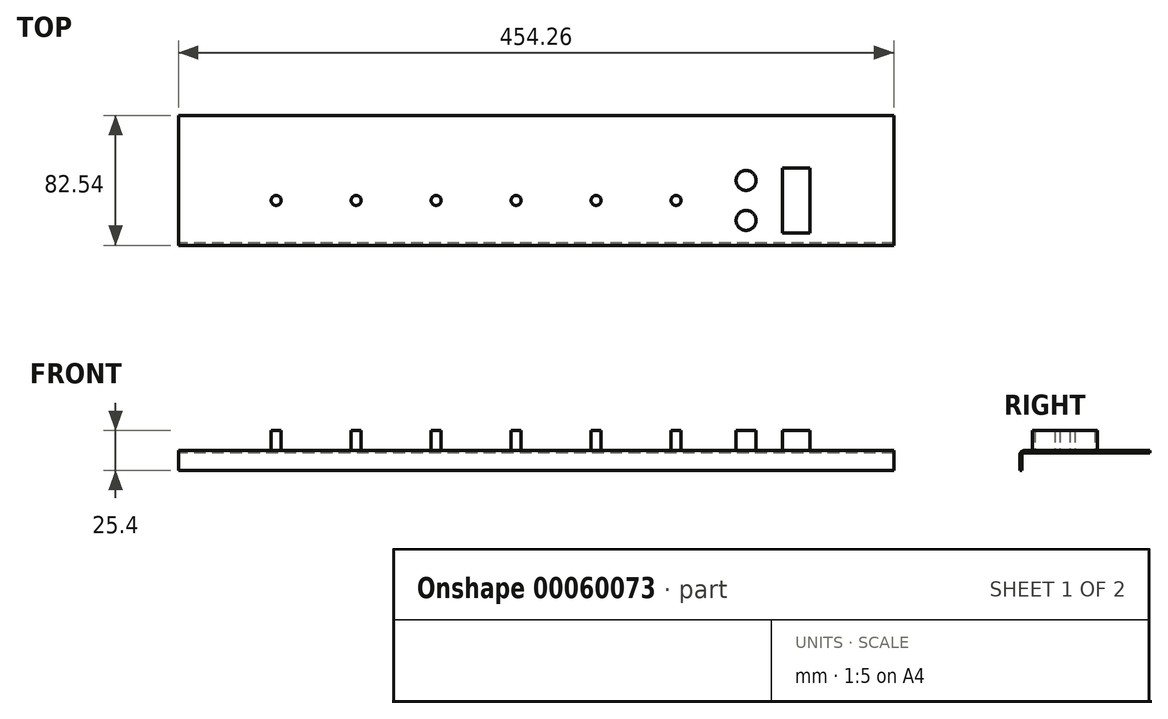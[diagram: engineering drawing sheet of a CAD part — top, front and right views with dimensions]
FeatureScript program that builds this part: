
annotation { "Feature Type Name" : "Feature", "Feature Type Description" : "" }
export const myFeature = defineFeature(function(context is Context, id is Id, definition is map)
    precondition{}
    {
        {
            var Q0;
            Q0=qCreatedBy(makeId("Top.planeOp"),FACE);
            var sketch = newSketch(context, id + "F0", { "sketchPlane" : qUnion([Q0])});
            skLineSegment(sketch, "E0.rect.bottom", {"start": v(241.3, -41.27) * mm, "end": v(-241.3, -41.28) * mm});
            skLineSegment(sketch, "E0.rect.top", {"start": v(241.3, 41.28) * mm, "end": v(-241.3, 41.27) * mm});
            skLineSegment(sketch, "E0.rect.left", {"start": v(241.3, -41.27) * mm, "end": v(241.3, 41.28) * mm});
            skLineSegment(sketch, "E0.rect.right", {"start": v(-241.3, -41.28) * mm, "end": v(-241.3, 41.27) * mm});
            skPoint(sketch, "E0.rect.middle", {"position": v(0, 0) * mm});
            skSolve(sketch);
        }
        {
            var Q0;
            Q0 = qSketchRegion(id + "F0", true);
            extrude(context, id + "F1", {"entities" : qUnion([Q0]), "oppositeDirection" : true, "depth" : 12.7 * mm});
        }
        {
            var Q0;
            Q0=makeQuery(id+"F1.opExtrude","CAP_EDGE",EDGE,{"disambiguationData":[OSD([sQuery(id+"F0.wireOp",EDGE,"E0.rect.bottom")])],"isStart":true});
            fillet(context, id + "F2", {"entities" : qUnion([Q0]), "radius" : 3.17 * mm, "tangentPropagation" : true, "allowEdgeOverflow" : false});
        }
        {
            var Q0;
            Q0=makeQuery(id+"F1.opExtrude","CAP_FACE",FACE,{"disambiguationData":[OSD([sQuery(id+"F0.wireOp",EDGE,"E0.rect.bottom"),sQuery(id+"F0.wireOp",EDGE,"E0.rect.top"),sQuery(id+"F0.wireOp",EDGE,"E0.rect.left"),sQuery(id+"F0.wireOp",EDGE,"E0.rect.right")])],"isStart":false});
            var Q1;
            Q1=makeQuery(id+"F1.opExtrude","SWEPT_FACE",FACE,{"disambiguationData":[OSD([sQuery(id+"F0.wireOp",EDGE,"E0.rect.left")])]});
            var Q2;
            Q2=makeQuery(id+"F1.opExtrude","SWEPT_FACE",FACE,{"disambiguationData":[OSD([sQuery(id+"F0.wireOp",EDGE,"E0.rect.top")])]});
            var Q3;
            Q3=makeQuery(id+"F1.opExtrude","SWEPT_FACE",FACE,{"disambiguationData":[OSD([sQuery(id+"F0.wireOp",EDGE,"E0.rect.right")])]});
            shell(context, id + "F3", {"entities" : qUnion([Q0, Q1, Q2, Q3]), "thickness" : 1.52 * mm});
        }
        {
            var Q0;
            Q0=makeQuery(id+"F1.opExtrude","CAP_FACE",FACE,{"disambiguationData":[OSD([sQuery(id+"F0.wireOp",EDGE,"E0.rect.bottom"),sQuery(id+"F0.wireOp",EDGE,"E0.rect.top"),sQuery(id+"F0.wireOp",EDGE,"E0.rect.left"),sQuery(id+"F0.wireOp",EDGE,"E0.rect.right")])],"isStart":true});
            var sketch = newSketch(context, id + "F4", { "sketchPlane" : qUnion([Q0])});
            skCircle(sketch, "E1", {"center": v(-114.3, -12.7) * mm, "radius": 3.18 * mm});
            skCircle(sketch, "E2", {"center": v(-63.5, -12.7) * mm, "radius": 3.18 * mm});
            skCircle(sketch, "E3", {"center": v(-12.7, -12.7) * mm, "radius": 3.18 * mm});
            skCircle(sketch, "E4", {"center": v(38.1, -12.7) * mm, "radius": 3.18 * mm});
            skCircle(sketch, "E5", {"center": v(88.9, -12.7) * mm, "radius": 3.18 * mm});
            skCircle(sketch, "E6", {"center": v(-165.1, -12.7) * mm, "radius": 3.18 * mm});
            skCircle(sketch, "E7", {"center": v(133.35, 0) * mm, "radius": 6.35 * mm});
            skCircle(sketch, "E8", {"center": v(133.35, -25.4) * mm, "radius": 6.35 * mm});
            skLineSegment(sketch, "E9.bottom", {"start": v(173.83, 7.94) * mm, "end": v(156.37, 7.94) * mm});
            skLineSegment(sketch, "E9.top", {"start": v(173.83, -33.34) * mm, "end": v(156.37, -33.34) * mm});
            skLineSegment(sketch, "E9.left", {"start": v(173.83, 7.94) * mm, "end": v(173.83, -33.34) * mm});
            skLineSegment(sketch, "E9.right", {"start": v(156.37, 7.94) * mm, "end": v(156.37, -33.34) * mm});
            skLineSegment(sketch, "E10", {"start": v(-165.1, -12.7) * mm, "end": v(-114.3, -12.7) * mm, "construction": true});
            skLineSegment(sketch, "E11", {"start": v(-63.5, -12.7) * mm, "end": v(-12.7, -12.7) * mm, "construction": true});
            skLineSegment(sketch, "E12", {"start": v(38.1, -12.7) * mm, "end": v(88.9, -12.7) * mm, "construction": true});
            skLineSegment(sketch, "E13", {"start": v(38.1, -12.7) * mm, "end": v(-12.7, -12.7) * mm, "construction": true});
            skLineSegment(sketch, "E14", {"start": v(-63.5, -12.7) * mm, "end": v(-114.3, -12.7) * mm, "construction": true});
            skLineSegment(sketch, "E15", {"start": v(88.9, -12.7) * mm, "end": v(156.37, -12.7) * mm, "construction": true});
            skLineSegment(sketch, "E16", {"start": v(165.1, -33.34) * mm, "end": v(165.1, 7.94) * mm, "construction": true});
            skSolve(sketch);
        }
        {
            var Q0;
            Q0 = qSketchRegion(id + "F4", true);
            extrude(context, id + "F5", {"entities" : qUnion([Q0]), "operationType" : NewBodyOperationType.ADD, "depth" : 12.7 * mm});
        }
        {
            var Q0;
            Q0=makeQuery(id+"F1.opExtrude","CAP_FACE",FACE,{"disambiguationData":[OSD([sQuery(id+"F0.wireOp",EDGE,"E0.rect.bottom"),sQuery(id+"F0.wireOp",EDGE,"E0.rect.top"),sQuery(id+"F0.wireOp",EDGE,"E0.rect.left"),sQuery(id+"F0.wireOp",EDGE,"E0.rect.right")])],"isStart":true});
            var sketch = newSketch(context, id + "F6", { "sketchPlane" : qUnion([Q0])});
            skLineSegment(sketch, "E17.bottom", {"start": v(-241.3, 41.27) * mm, "end": v(-227.13, 41.27) * mm});
            skLineSegment(sketch, "E17.top", {"start": v(-241.3, -41.28) * mm, "end": v(-227.13, -41.28) * mm});
            skLineSegment(sketch, "E17.left", {"start": v(-241.3, 41.27) * mm, "end": v(-241.3, -41.28) * mm});
            skLineSegment(sketch, "E17.right", {"start": v(-227.13, 41.27) * mm, "end": v(-227.13, -41.28) * mm});
            skLineSegment(sketch, "E18.bottom", {"start": v(241.3, 41.28) * mm, "end": v(227.13, 41.28) * mm});
            skLineSegment(sketch, "E18.top", {"start": v(241.3, -41.27) * mm, "end": v(227.13, -41.27) * mm});
            skLineSegment(sketch, "E18.left", {"start": v(241.3, 41.28) * mm, "end": v(241.3, -41.27) * mm});
            skLineSegment(sketch, "E18.right", {"start": v(227.13, 41.28) * mm, "end": v(227.13, -41.27) * mm});
            skSolve(sketch);
        }
        {
            var Q0;
            Q0 = qSketchRegion(id + "F6", true);
            extrude(context, id + "F7", {"entities" : qUnion([Q0]), "operationType" : NewBodyOperationType.REMOVE, "oppositeDirection" : true, "depth" : 25.4 * mm});
        }
    });
